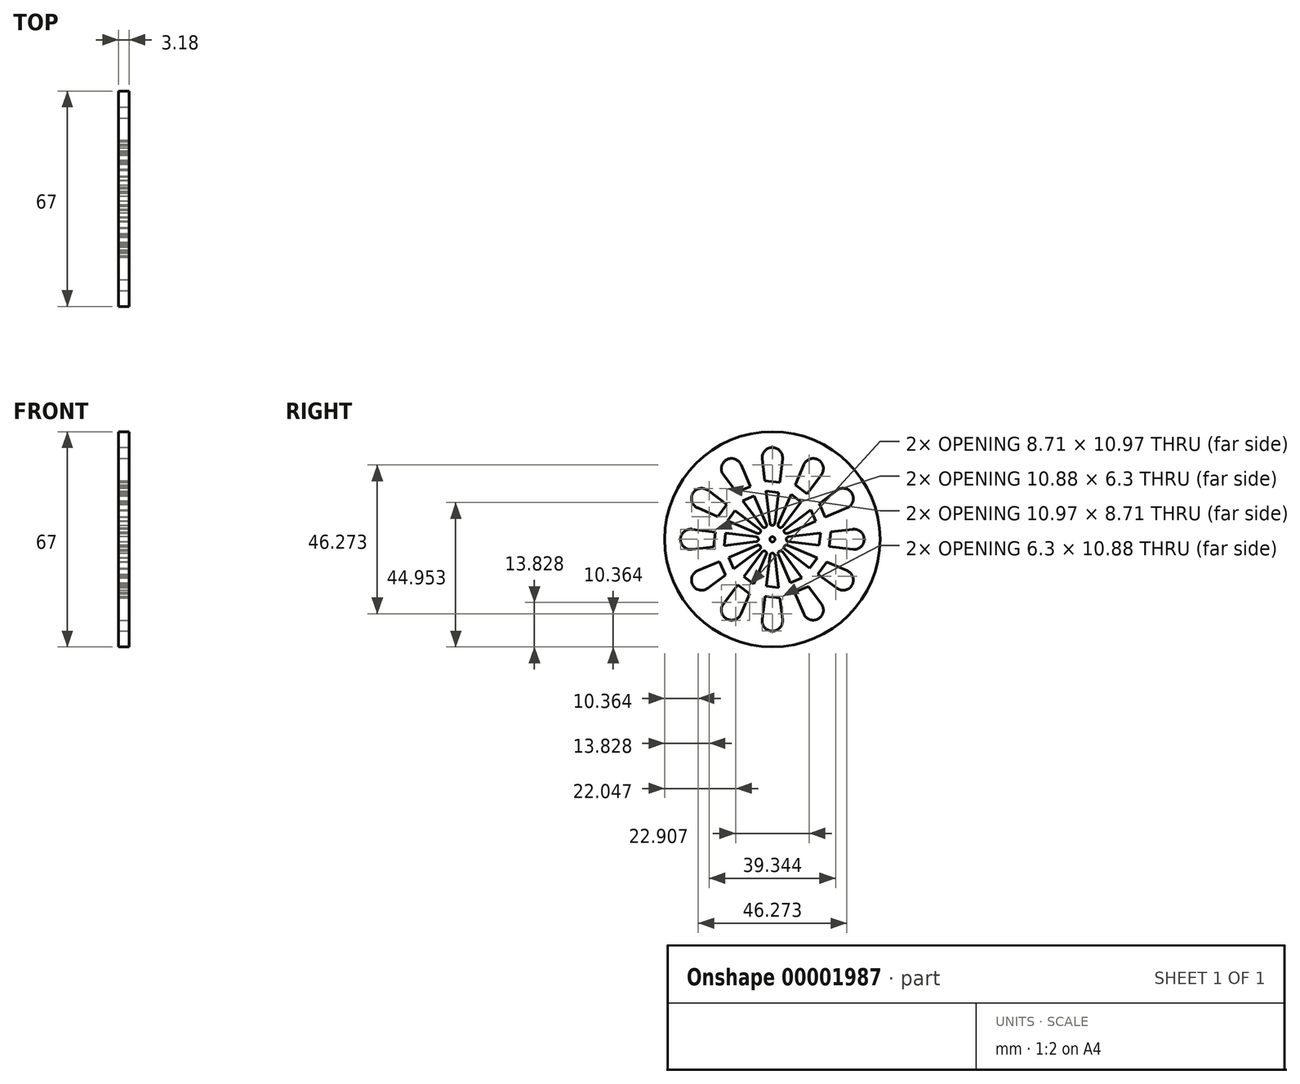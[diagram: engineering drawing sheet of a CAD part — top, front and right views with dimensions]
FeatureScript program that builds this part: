
annotation { "Feature Type Name" : "Feature", "Feature Type Description" : "" }
export const myFeature = defineFeature(function(context is Context, id is Id, definition is map)
    precondition{}
    {
        {
            var Q0;
            Q0=qCreatedBy(makeId("Right.planeOp"),FACE);
            var sketch = newSketch(context, id + "F0", { "sketchPlane" : qUnion([Q0])});
            skCircle(sketch, "E0", {"center": v(0, 0) * mm, "radius": 33.5 * mm});
            skLineSegment(sketch, "E1", {"start": v(-33.5, 0) * mm, "end": v(33.5, 0) * mm, "construction": true});
            skCircle(sketch, "E2", {"center": v(0, 0) * mm, "radius": 0.8 * mm});
            skSolve(sketch);
        }
        {
            var Q0;
            Q0=makeQuery(id+"F0.imprint","IMPRINT",FACE,{"disambiguationData":[TD([[makeQuery(id+"F0.imprint","IMPRINT",EDGE,{"derivedFrom":sQuery(id+"F0.wireOp",EDGE,"E0")}),1.0]])]});
            extrude(context, id + "F1", {"entities" : qUnion([Q0]), "depth" : 3.17 * mm});
        }
        {
            var Q0;
            Q0=makeQuery(id+"F1.opExtrude","CAP_FACE",FACE,{"disambiguationData":[OSD([sQuery(id+"F0.wireOp",EDGE,"E0"),sQuery(id+"F0.wireOp",EDGE,"E2")])],"isStart":false});
            var sketch = newSketch(context, id + "F2", { "sketchPlane" : qUnion([Q0])});
            skArc(sketch, "E3", {"start": v(3.15, 25.02) * mm, "mid": v(0, 28.58) * mm, "end": v(-3.15, 25.02) * mm});
            skArc(sketch, "E4", {"start": v(-0.76, 4.99) * mm, "mid": v(0, 4.32) * mm, "end": v(0.76, 4.99) * mm});
            skLineSegment(sketch, "E5", {"start": v(3.15, 25.02) * mm, "end": v(0.76, 4.99) * mm});
            skLineSegment(sketch, "E6", {"start": v(-0.76, 4.99) * mm, "end": v(-3.15, 25.02) * mm});
            skLineSegment(sketch, "E7", {"start": v(-2.34, 18.25) * mm, "end": v(2.28, 17.7) * mm});
            skLineSegment(sketch, "E8", {"start": v(-1.95, 15) * mm, "end": v(1.9, 14.55) * mm});
            skSolve(sketch);
        }
        {
            var Q0;
            {var subQ2=sQuery(id+"F2.wireOp",EDGE,"E3");Q0=makeQuery(id+"F2.imprint","IMPRINT",FACE,{"disambiguationData":[TD([[makeQuery(id+"F2.imprint","IMPRINT",EDGE,{"derivedFrom":subQ2}),1.0]])]});}
            var Q1;
            {var subQ2=sQuery(id+"F2.wireOp",EDGE,"E4");Q1=makeQuery(id+"F2.imprint","IMPRINT",FACE,{"disambiguationData":[TD([[makeQuery(id+"F2.imprint","IMPRINT",EDGE,{"derivedFrom":subQ2}),1.0]])]});}
            extrude(context, id + "F3", {"entities" : qUnion([Q0, Q1]), "operationType" : NewBodyOperationType.REMOVE, "endBound" : BoundingType.UP_TO_NEXT, "oppositeDirection" : true, "depth" : 25.4 * mm});
        }
        {
            var Q0;
            Q0=makeQuery(id+"F3.boolean.opBoolean","COPY",FACE,{"derivedFrom":makeQuery(id+"F3.opExtrude","SWEPT_FACE",FACE,{"disambiguationData":[OSD([sQuery(id+"F2.wireOp",EDGE,"E3")])]})});
            var Q1;
            {var subQ0=sQuery(id+"F2.wireOp",EDGE,"E5");Q1=qUnion([makeQuery(id+"F3.boolean.opBoolean","COPY",FACE,{"derivedFrom":makeQuery(id+"F3.opExtrude","SWEPT_FACE",FACE,{"disambiguationData":[OSD([subQ0]),TDD([makeQuery(id+"F2.imprint","IMPRINT",EDGE,{"disambiguationData":[TD([[makeQuery(id+"F2.imprint","INTERSECT",VERTEX,{"derivedFrom":[sQuery(id+"F2.wireOp",EDGE,"E3"),subQ0]}),-1.0]])],"derivedFrom":subQ0})])]})}),makeQuery(id+"F3.boolean.opBoolean","COPY",FACE,{"derivedFrom":makeQuery(id+"F3.opExtrude","SWEPT_FACE",FACE,{"disambiguationData":[OSD([subQ0]),TDD([makeQuery(id+"F2.imprint","IMPRINT",EDGE,{"disambiguationData":[TD([[makeQuery(id+"F2.imprint","INTERSECT",VERTEX,{"derivedFrom":[sQuery(id+"F2.wireOp",EDGE,"E4"),subQ0]}),1.0]])],"derivedFrom":subQ0})])]})})]);}
            var Q2;
            {var subQ0=sQuery(id+"F2.wireOp",EDGE,"E6");Q2=qUnion([makeQuery(id+"F3.boolean.opBoolean","COPY",FACE,{"derivedFrom":makeQuery(id+"F3.opExtrude","SWEPT_FACE",FACE,{"disambiguationData":[OSD([subQ0]),TDD([makeQuery(id+"F2.imprint","IMPRINT",EDGE,{"disambiguationData":[TD([[makeQuery(id+"F2.imprint","INTERSECT",VERTEX,{"derivedFrom":[sQuery(id+"F2.wireOp",EDGE,"E4"),subQ0]}),-1.0]])],"derivedFrom":subQ0})])]})}),makeQuery(id+"F3.boolean.opBoolean","COPY",FACE,{"derivedFrom":makeQuery(id+"F3.opExtrude","SWEPT_FACE",FACE,{"disambiguationData":[OSD([subQ0]),TDD([makeQuery(id+"F2.imprint","IMPRINT",EDGE,{"disambiguationData":[TD([[makeQuery(id+"F2.imprint","INTERSECT",VERTEX,{"derivedFrom":[sQuery(id+"F2.wireOp",EDGE,"E3"),subQ0]}),1.0]])],"derivedFrom":subQ0})])]})})]);}
            var Q3;
            Q3=makeQuery(id+"F3.boolean.opBoolean","COPY",FACE,{"derivedFrom":makeQuery(id+"F3.opExtrude","SWEPT_FACE",FACE,{"disambiguationData":[OSD([sQuery(id+"F2.wireOp",EDGE,"E4")])]})});
            var Q4;
            Q4=makeQuery(id+"F3.boolean.opBoolean","COPY",FACE,{"derivedFrom":makeQuery(id+"F3.opExtrude","SWEPT_FACE",FACE,{"disambiguationData":[OSD([sQuery(id+"F2.wireOp",EDGE,"E7")])]})});
            var Q5;
            Q5=makeQuery(id+"F3.boolean.opBoolean","COPY",FACE,{"derivedFrom":makeQuery(id+"F3.opExtrude","SWEPT_FACE",FACE,{"disambiguationData":[OSD([sQuery(id+"F2.wireOp",EDGE,"E8")])]})});
            var Q6;
            Q6=makeQuery(id+"F1.opExtrude","CAP_EDGE",EDGE,{"disambiguationData":[OSD([sQuery(id+"F0.wireOp",EDGE,"E2")])],"isStart":false});
            circularPattern(context, id + "F4", {"faces" : qUnion([Q0, Q1, Q2, Q3, Q4, Q5]), "axis" : qUnion([Q6]), "angle" : 30 * degree, "instanceCount" : 12, "patternType" : PatternType.FACE});
        }
    });
